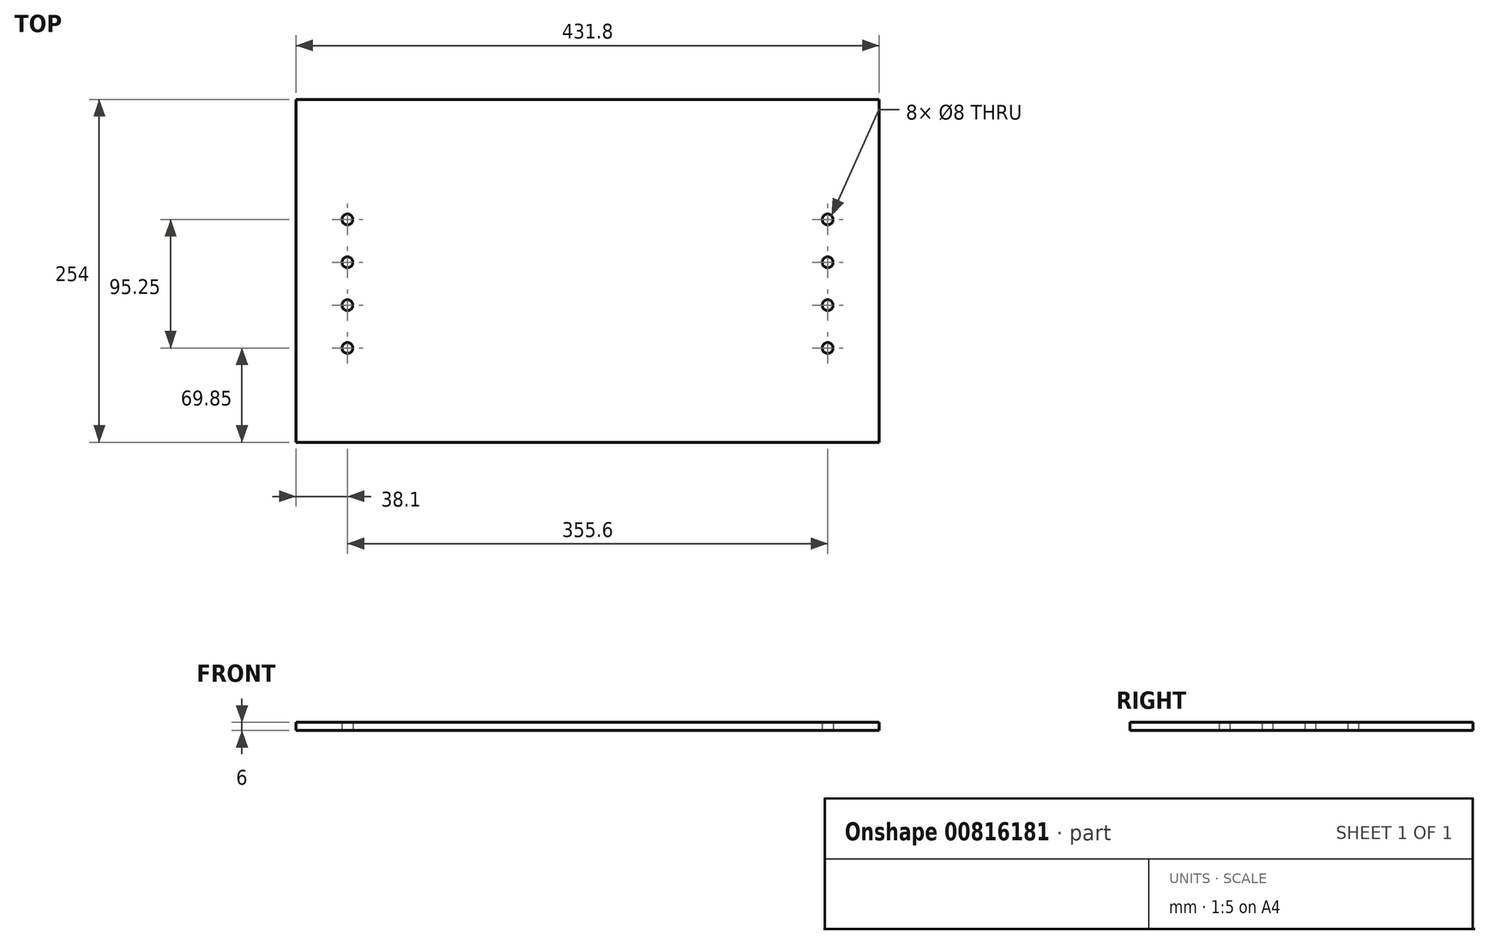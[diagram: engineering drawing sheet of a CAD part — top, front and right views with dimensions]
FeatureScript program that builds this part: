
annotation { "Feature Type Name" : "Feature", "Feature Type Description" : "" }
export const myFeature = defineFeature(function(context is Context, id is Id, definition is map)
    precondition{}
    {
        {
            var Q0;
            Q0=qCreatedBy(makeId("Top.planeOp"),FACE);
            var sketch = newSketch(context, id + "F0", { "sketchPlane" : qUnion([Q0])});
            skLineSegment(sketch, "E0.bottom", {"start": v(-215.9, 127) * mm, "end": v(215.9, 127) * mm});
            skLineSegment(sketch, "E0.top", {"start": v(-215.9, -127) * mm, "end": v(215.9, -127) * mm});
            skLineSegment(sketch, "E0.left", {"start": v(-215.9, 127) * mm, "end": v(-215.9, -127) * mm});
            skLineSegment(sketch, "E0.right", {"start": v(215.9, 127) * mm, "end": v(215.9, -127) * mm});
            skPoint(sketch, "E0.middle", {"position": v(0, 0) * mm});
            skCircle(sketch, "E1", {"center": v(177.8, 38.1) * mm, "radius": 4 * mm});
            skCircle(sketch, "E2", {"center": v(177.8, 6.35) * mm, "radius": 4 * mm});
            skLineSegment(sketch, "E3", {"start": v(0, 127) * mm, "end": v(0, -127) * mm, "construction": true});
            skCircle(sketch, "E4.MirrorC", {"center": v(-177.8, 38.1) * mm, "radius": 4 * mm});
            skCircle(sketch, "E5.MirrorC", {"center": v(-177.8, 6.35) * mm, "radius": 4 * mm});
            skLineSegment(sketch, "E6", {"start": v(-215.9, 0) * mm, "end": v(215.9, 0) * mm, "construction": true});
            skCircle(sketch, "E7", {"center": v(177.8, -25.4) * mm, "radius": 4 * mm});
            skCircle(sketch, "E8", {"center": v(177.8, -57.15) * mm, "radius": 4 * mm});
            skCircle(sketch, "E9.MirrorC", {"center": v(-177.8, -57.15) * mm, "radius": 4 * mm});
            skCircle(sketch, "E10.MirrorC", {"center": v(-177.8, -25.4) * mm, "radius": 4 * mm});
            skSolve(sketch);
        }
        {
            var Q0;
            Q0=makeQuery(id+"F0.imprint","IMPRINT",FACE,{"disambiguationData":[TD([[makeQuery(id+"F0.imprint","IMPRINT",EDGE,{"derivedFrom":sQuery(id+"F0.wireOp",EDGE,"E0.bottom")}),-1.0]])]});
            extrude(context, id + "F1", {"entities" : qUnion([Q0]), "endBound" : BoundingType.SYMMETRIC, "depth" : 6 * mm, "offsetDistance" : 25 * mm});
        }
    });
